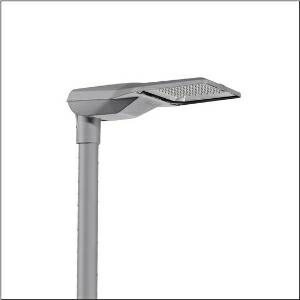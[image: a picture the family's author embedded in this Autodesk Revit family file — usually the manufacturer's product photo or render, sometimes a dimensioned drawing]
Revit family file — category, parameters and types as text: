
# Revit family: streetlight_sl_21_iq_midi___p0_5a_5xe3v31d08nb_4594
name_source: partatom
category: Lighting Fixtures
units: mm (PartAtom-declared; Revit-internal decimal feet)

## family parameters
Cut with Voids When Loaded = No
Host = Face
Light Source = No
Part Type = Normal
Room Calculation Point = No
Round Connector Dimension = Use Diameter
Shared = No

## types (1)
- --- (1 x LED, 22830 lm, 155.5 W, 3000K)
    Apparent Load = 155 VA
    CIE Flux Codes = 37 73 96 100 100
    Color Rendering = 70
    Color Temperature = 3000K
    Default Elevation = 1800 mm
    Description = Streetlight SL 21 iQ midi, mast luminaire, primary light control with lens, of PMMA, primary optical cover: cover, of toughened safety glass, transparent, light distribution: P0.5a, light emission: direct distribution, primary light characteristic: asymmetric, installation type: post-top, side-entry, LED, High Power LED, rated luminous flux: 22.830lm, luminous efficacy: 147lm/W, light colour: 730, colour temperature: 3000K, control gear: iQ-Comfort, control: pre-setting: linear dimming characteristic, Auto-Match, Temp-Guard, Lumen-Switch, Night-Set, Smart-Wire, Light-Fading, Desk-Remote (wireless, voltage-free reading and setting of iQ features in the workshop via application-optimized NFC function/RFID function), optimised constant luminous flux control (CLO 2.0), mains connection: 230..240V, AC, 50/60Hz, start of lifetime: 156W, end of service life: 162W, reduction: 69W, luminaire housing, of diecast aluminium, powder-coated, SITECO metallic grey (DB 702S), corrosivity category C5 high according to DIN EN ISO 12944, please order mast flange separately, inclination adjustable: 0°, 5°, 10°, 15°, sealing non-destructively replaceable, multi-level sealing system, length: 644mm, width: 335mm, height: 110mm, mast flange for spigot size: 42mm (side-entry): 5XC10008XM4, 60/48mm (side-entry/post-top): 5XC10108XM2, 76/60mm (side-entry/post-top): 5XC10108XM1, mounting height: 4..8m, protection rating (complete): IP66, insulation class (complete): insulation class II (safety insulation), certification: CE, ENEC, ENEC+, VDE, impact resistance: IK10, permissible operating ambient temperature for outdoor applications: -40..+50°C, standard-compliant lighting for roads and squares, packaging unit: 1 piece

Light Distribution: P0.5a
    Height = 111 mm
    Lamp = 1 x LED
    Lamp Light Flux = 22830 lm
    Lamp Power = 155.5 W
    Lamp count = 1
    Length = 644 mm
    Luminous efficacy = 147 lm/W
    Manufacturer = Siteco
    ModVariant = No
    Model = 5XE3V31D08NB
    Number of Poles = 1
    OnlyDefault = Yes
    Power Factor = 1
    Product Name = Streetlight SL 21 iQ midi | P0.5a
    Product group = mast luminaire | pylon top
    ProductGroupID = 6100
    Protection Class = Protection class II
    Protection Degree = IP 66
    RLX_Detail_Level = 1
    RLX_Emergency_Light_Flux = 0 lm
    RLX_Emergency_Type = 0
    RLX_Emergency_Type_DB = No
    RlxData = <blob elided: 91277 chars, md5=7fd3ae1e>
    Socket = socket
    Standby Power = 0 W
    System Light Flux = 22831 lm
    System Power = 155 W
    Type Comments = factory setting: luminous flux: 100 % | dim-lin: 254 | 823 mA
    Type Image = l_1004298.jpg
    URL = http://relux.com
    VarID = @adj_076899
    Voltage = 0 V
    Weight = 0.00 kg
    Width = 336 mm

## geometry (parser evidence)
native form markers: Blend x4, Sweep x12
no freeform markers — native parametric forms only
